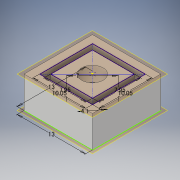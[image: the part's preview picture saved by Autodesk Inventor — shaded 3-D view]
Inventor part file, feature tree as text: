
AUTODESK INVENTOR PART (.ipt)
format: ipt  version: 2019 (Build 230136000, 136)  size: 134,656 bytes
history: native  units: in
note: dims shown in document units (in); Inventor stores cm internally (conversion verified against a paired STEP export)
features: extrude x4, sketch x2, other x1
ambient origin geometry x8: Origin, YZ Plane, XZ Plane, XY Plane, X Axis, Y Axis, Z Axis, Center Point
bodies: Body1 (feature_tree)
feature tree (7):
  other  "作業平面2"
  sketch  "スケッチ3"
  sketch  "スケッチ1"
  extrude  "押し出し8"  Depth=0.2362in
  extrude  "押し出し9"  Depth=0.313in
  extrude  "押し出し10"  Depth=0.313in
  extrude  "押し出し11"  Depth=0.3957in
